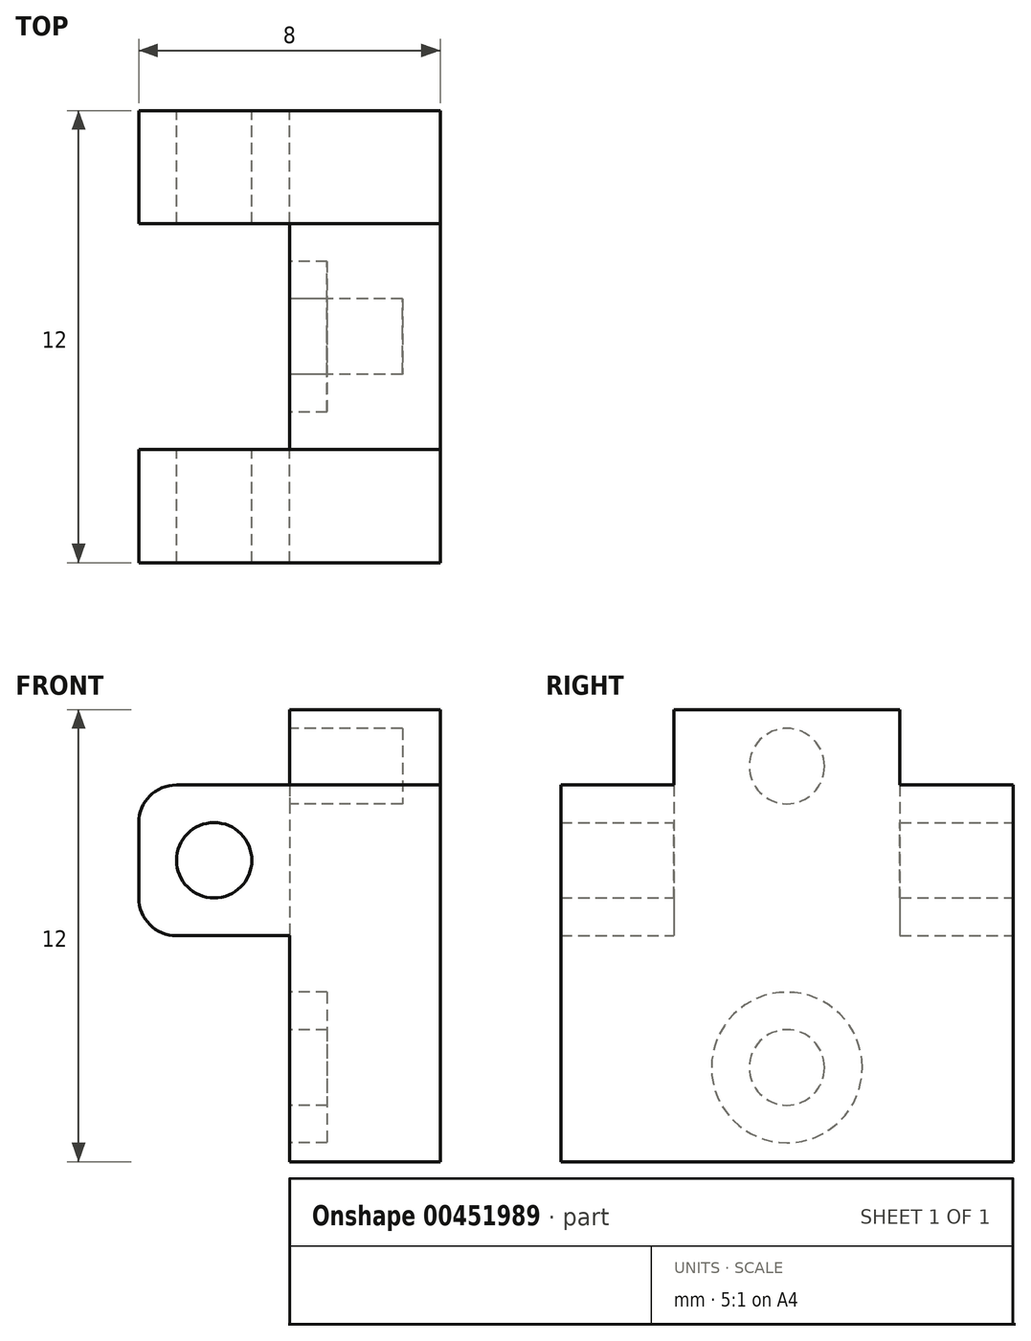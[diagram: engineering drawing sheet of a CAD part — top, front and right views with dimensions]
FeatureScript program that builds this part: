
annotation { "Feature Type Name" : "Feature", "Feature Type Description" : "" }
export const myFeature = defineFeature(function(context is Context, id is Id, definition is map)
    precondition{}
    {
        {
            var Q0;
            Q0=qCreatedBy(makeId("Front.planeOp"),FACE);
            var sketch = newSketch(context, id + "F0", { "sketchPlane" : qUnion([Q0])});
            skLineSegment(sketch, "E0.bottom", {"start": v(0, 0) * mm, "end": v(4, 0) * mm});
            skLineSegment(sketch, "E0.top", {"start": v(0, 10) * mm, "end": v(4, 10) * mm});
            skLineSegment(sketch, "E0.left", {"start": v(0, 0) * mm, "end": v(0, 6) * mm});
            skLineSegment(sketch, "E0.right", {"start": v(4, 0) * mm, "end": v(4, 10) * mm});
            skLineSegment(sketch, "E1.bottom", {"start": v(4, 10) * mm, "end": v(-4, 10) * mm});
            skLineSegment(sketch, "E1.top", {"start": v(0, 6) * mm, "end": v(-4, 6) * mm});
            skLineSegment(sketch, "E1.left", {"start": v(4, 10) * mm, "end": v(4, 6) * mm});
            skLineSegment(sketch, "E1.right", {"start": v(-4, 10) * mm, "end": v(-4, 6) * mm});
            skLineSegment(sketch, "E2", {"start": v(-4, 6) * mm, "end": v(0, 10) * mm, "construction": true});
            skCircle(sketch, "E3", {"center": v(-2, 8) * mm, "radius": 1 * mm});
            skSolve(sketch);
        }
        {
            var Q0;
            Q0 = qSketchRegion(id + "F0", true);
            extrude(context, id + "F1", {"entities" : qUnion([Q0]), "depth" : 6 * mm, "hasSecondDirection" : true, "secondDirectionOppositeDirection" : true, "secondDirectionDepth" : 6 * mm});
        }
        {
            var Q0;
            Q0=makeQuery(id+"F1.opExtrude","SWEPT_EDGE",EDGE,{"disambiguationData":[OSD([sQuery(id+"F0.wireOp",EDGE,"E1.bottom"),sQuery(id+"F0.wireOp",EDGE,"E1.right")])]});
            var Q1;
            Q1=makeQuery(id+"F1.opExtrude","SWEPT_EDGE",EDGE,{"disambiguationData":[OSD([sQuery(id+"F0.wireOp",EDGE,"E1.top"),sQuery(id+"F0.wireOp",EDGE,"E1.right")])]});
            fillet(context, id + "F2", {"entities" : qUnion([Q0, Q1]), "radius" : 1 * mm, "tangentPropagation" : true, "allowEdgeOverflow" : false});
        }
        {
            var Q0;
            Q0=makeQuery(id+"F1.opExtrude","SWEPT_FACE",FACE,{"disambiguationData":[OSD([sQuery(id+"F0.wireOp",EDGE,"E1.right")])]});
            var sketch = newSketch(context, id + "F3", { "sketchPlane" : qUnion([Q0])});
            skLineSegment(sketch, "E4.bottom", {"start": v(-3, 6) * mm, "end": v(3, 6) * mm});
            skLineSegment(sketch, "E4.top", {"start": v(-3, 10) * mm, "end": v(3, 10) * mm});
            skLineSegment(sketch, "E4.left", {"start": v(-3, 6) * mm, "end": v(-3, 10) * mm});
            skLineSegment(sketch, "E4.right", {"start": v(3, 6) * mm, "end": v(3, 10) * mm});
            skSolve(sketch);
        }
        {
            var Q0;
            Q0 = qSketchRegion(id + "F3", true);
            var Q1;
            Q1=makeQuery(id+"F1.opExtrude","SWEPT_FACE",FACE,{"disambiguationData":[OSD([sQuery(id+"F0.wireOp",EDGE,"E0.left")])]});
            extrude(context, id + "F4", {"entities" : qUnion([Q0]), "operationType" : NewBodyOperationType.REMOVE, "endBound" : BoundingType.UP_TO_SURFACE, "oppositeDirection" : true, "endBoundEntityFace" : qUnion([Q1]), "depth" : 25 * mm});
        }
        {
            var Q0;
            {var subQ0=sQuery(id+"F0.wireOp",EDGE,"E0.left");Q0=makeQuery(id+"F4.boolean.opBoolean","MERGE",FACE,{"derivedFrom":[makeQuery(id+"F1.opExtrude","SWEPT_FACE",FACE,{"disambiguationData":[OSD([subQ0])]}),makeQuery(id+"F4.opExtrude","CAP_FACE",FACE,{"disambiguationData":[OSD([subQ0])],"isStart":false})]});}
            var sketch = newSketch(context, id + "F5", { "sketchPlane" : qUnion([Q0])});
            skCircle(sketch, "E5", {"center": v(0, 2.5) * mm, "radius": 1 * mm});
            skCircle(sketch, "E6", {"center": v(0, 2.5) * mm, "radius": 2 * mm});
            skSolve(sketch);
        }
        {
            var Q0;
            Q0 = qSketchRegion(id + "F5", true);
            extrude(context, id + "F6", {"entities" : qUnion([Q0]), "operationType" : NewBodyOperationType.REMOVE, "oppositeDirection" : true, "depth" : 1 * mm});
        }
        {
            var Q0;
            Q0=makeQuery(id+"F1.opExtrude","SWEPT_FACE",FACE,{"disambiguationData":[OSD([sQuery(id+"F0.wireOp",EDGE,"E1.bottom")])]});
            var sketch = newSketch(context, id + "F7", { "sketchPlane" : qUnion([Q0])});
            skLineSegment(sketch, "E7.bottom", {"start": v(0, 3) * mm, "end": v(4, 3) * mm});
            skLineSegment(sketch, "E7.top", {"start": v(0, -3) * mm, "end": v(4, -3) * mm});
            skLineSegment(sketch, "E7.left", {"start": v(0, 3) * mm, "end": v(0, -3) * mm});
            skLineSegment(sketch, "E7.right", {"start": v(4, 3) * mm, "end": v(4, -3) * mm});
            skSolve(sketch);
        }
        {
            var Q0;
            Q0 = qSketchRegion(id + "F7", true);
            extrude(context, id + "F8", {"entities" : qUnion([Q0]), "operationType" : NewBodyOperationType.ADD, "depth" : 2 * mm});
        }
        {
            var Q0;
            {var subQ6=sQuery(id+"F0.wireOp",EDGE,"E0.left");var subQ7=sQuery(id+"F0.wireOp",EDGE,"E0.bottom");Q0=makeQuery(id+"F8.boolean.opBoolean","MERGE",FACE,{"derivedFrom":[makeQuery(id+"F6.boolean.opBoolean","SPLIT",FACE,{"disambiguationData":[TD([makeQuery(id+"F1.opExtrude","SWEPT_FACE",FACE,{"disambiguationData":[OSD([subQ7])]})])],"derivedFrom":makeQuery(id+"F4.boolean.opBoolean","MERGE",FACE,{"derivedFrom":[makeQuery(id+"F1.opExtrude","SWEPT_FACE",FACE,{"disambiguationData":[OSD([subQ6])]}),makeQuery(id+"F4.opExtrude","CAP_FACE",FACE,{"disambiguationData":[OSD([subQ6])],"isStart":false})]})}),makeQuery(id+"F8.opExtrude","SWEPT_FACE",FACE,{"disambiguationData":[OSD([sQuery(id+"F7.wireOp",EDGE,"E7.left")])]})]});}
            var sketch = newSketch(context, id + "F9", { "sketchPlane" : qUnion([Q0])});
            skCircle(sketch, "E8", {"center": v(0, 10.5) * mm, "radius": 1 * mm});
            skSolve(sketch);
        }
        {
            var Q0;
            Q0 = qSketchRegion(id + "F9", true);
            extrude(context, id + "F10", {"entities" : qUnion([Q0]), "operationType" : NewBodyOperationType.REMOVE, "oppositeDirection" : true, "depth" : 3 * mm});
        }
    });
